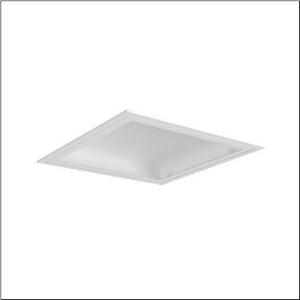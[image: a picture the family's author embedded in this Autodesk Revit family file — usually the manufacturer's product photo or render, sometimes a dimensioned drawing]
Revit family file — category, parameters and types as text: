
# Revit family: mira_r__21_51fr427a442a_c8f5
name_source: partatom
category: Lighting Fixtures
units: mm (PartAtom-declared; Revit-internal decimal feet)

## family parameters
Cut with Voids When Loaded = No
Host = Face
Light Source = No
Part Type = Normal
Room Calculation Point = No
Round Connector Dimension = Use Diameter
Shared = No

## types (1)
- Mira® 21 (1 x LED, 4860 lm, 37 W, 4000K)
    Apparent Load = 37 VA
    CIE Flux Codes = 50 81 97 100 100
    Color Rendering = 80
    Color Temperature = 4000K
    Default Elevation = 1800 mm
    Description = Mira® 21, clean room luminaire, primary light control with reflector, primary optical cover: cover, of PC, light emission: direct distribution, primary light characteristic: symmetric, installation type: recessed, LED, rated luminous flux: 4.860lm, luminous efficacy: 131lm/W, light colour: 840, colour temperature: 4000K, control gear: ON/OFF, with terminal, 3-pole, max. 2.5mm², mains connection: 230V, AC, 50/60Hz, rated input power: 37W, luminaire housing, of sheet steel, coated, pure white (RAL 9010), with concealed spring brackets, module: M625, length: 623mm, width: 623mm, height: 115mm, protection rating (complete): IP54, insulation class (complete): insulation class I (protective earthing), certification: CE, UKCA, permissible operating ambient temperature: -5..+40°C, standard: EN 50419, packaging unit: 1 piece
    Height = 0 mm  [stored 0 ft]
    Lamp = 1 x LED
    Lamp Light Flux = 4860 lm
    Lamp Power = 37 W
    Lamp count = 1
    Length = 625 mm
    Luminous efficacy = 131 lm/W
    Manufacturer = Siteco
    ModVariant = No
    Model = 51FR427A442A
    Mounting Place = Ceiling
    Mounting Type = Recessed
    Number of Poles = 1
    OnlyDefault = Yes
    Power Factor = 1
    Product Name = Mira® 21
    Product group = clean room luminaire | ceiling recessed
    ProductGroupID = 402
    Protection Class = Protection class I
    Protection Degree = IP 54
    RLX_Detail_Level = 1
    RLX_Emergency_Light_Flux = 0 lm
    RLX_Emergency_Type = 0
    RLX_Emergency_Type_DB = No
    RlxData = <blob elided: 13405 chars, md5=77cd6c38>
    Socket = socket
    Standby Power = 0 W
    System Light Flux = 4860 lm
    System Power = 37 W
    Type Comments = Product without accessories
    Type Image = l_1007109.jpg
    URL = http://relux.com
    VarID = ---
    Voltage = 0 V
    Weight = 0.00 kg
    Width = 625 mm

note: [stored X ft] marks values corroborated as IEEE doubles in the binary element streams (Revit-internal decimal feet)

## geometry (parser evidence)
native form markers: Sweep x9
no freeform markers — native parametric forms only
